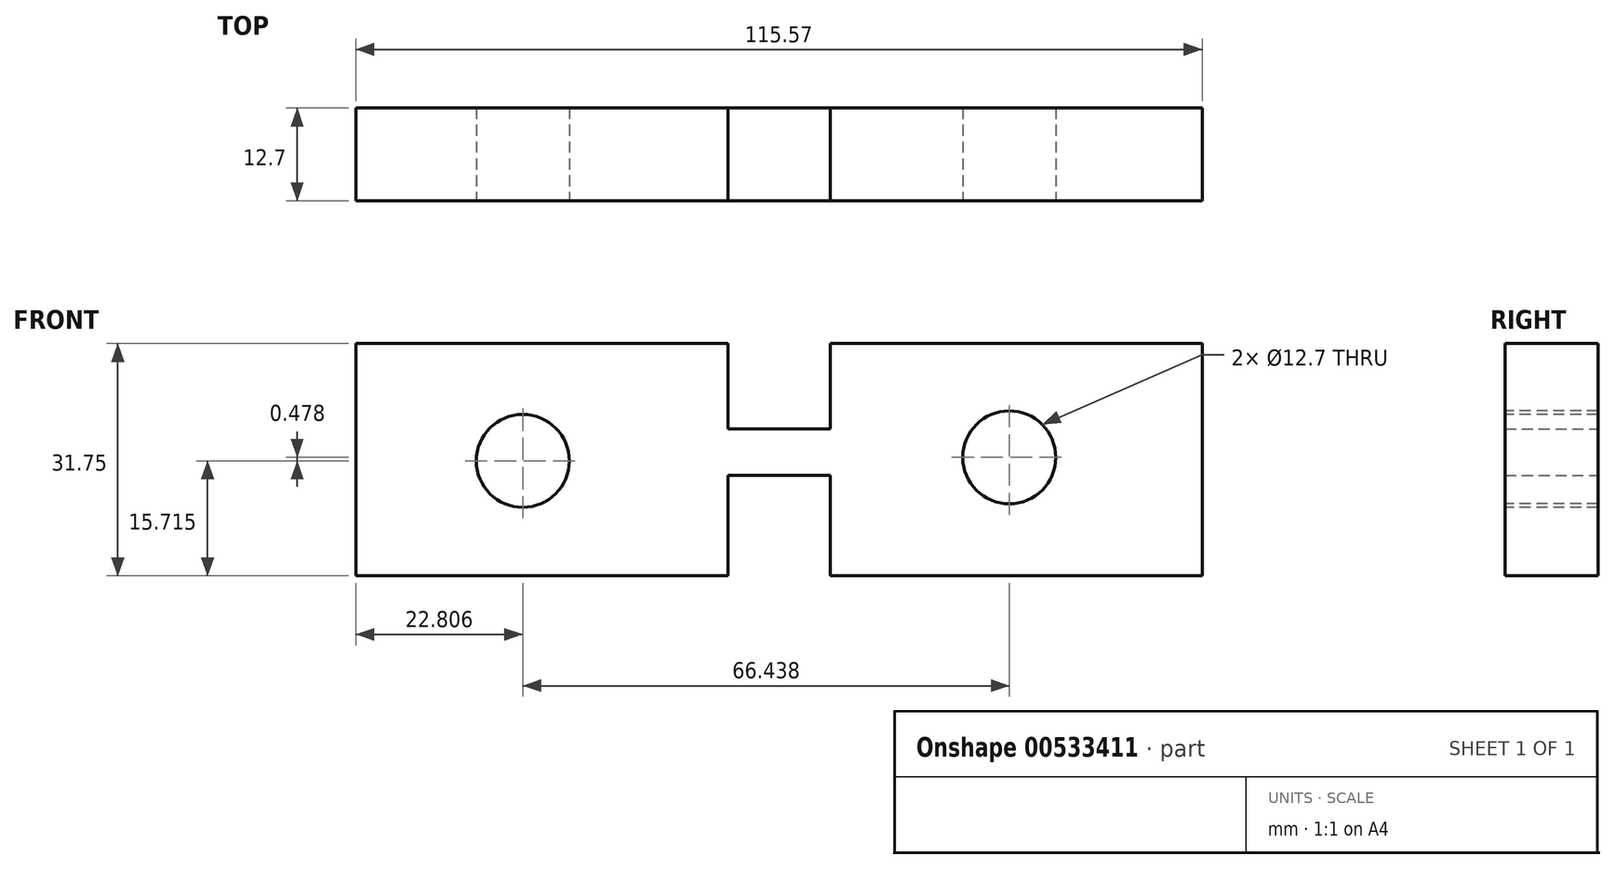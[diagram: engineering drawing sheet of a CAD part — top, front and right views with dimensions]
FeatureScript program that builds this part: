
annotation { "Feature Type Name" : "Feature", "Feature Type Description" : "" }
export const myFeature = defineFeature(function(context is Context, id is Id, definition is map)
    precondition{}
    {
        {
            var Q0;
            Q0=qCreatedBy(makeId("Front.planeOp"),FACE);
            var sketch = newSketch(context, id + "F0", { "sketchPlane" : qUnion([Q0])});
            skLineSegment(sketch, "E0", {"start": v(-13.97, 33.78) * mm, "end": v(0, 33.78) * mm});
            skLineSegment(sketch, "E1", {"start": v(0, 33.78) * mm, "end": v(0, 27.43) * mm});
            skLineSegment(sketch, "E2", {"start": v(0, 27.43) * mm, "end": v(-13.97, 27.43) * mm});
            skLineSegment(sketch, "E3.bottom", {"start": v(0, 45.47) * mm, "end": v(50.8, 45.47) * mm});
            skLineSegment(sketch, "E3.top", {"start": v(0, 13.72) * mm, "end": v(50.8, 13.72) * mm});
            skLineSegment(sketch, "E3.left", {"start": v(0, 45.47) * mm, "end": v(0, 13.72) * mm});
            skLineSegment(sketch, "E3.right", {"start": v(50.8, 45.47) * mm, "end": v(50.8, 13.72) * mm});
            skLineSegment(sketch, "E4", {"start": v(-13.97, 33.78) * mm, "end": v(-13.97, 27.43) * mm});
            skLineSegment(sketch, "E5.bottom", {"start": v(-13.97, 45.47) * mm, "end": v(-64.77, 45.47) * mm});
            skLineSegment(sketch, "E5.top", {"start": v(-13.97, 13.72) * mm, "end": v(-64.77, 13.72) * mm});
            skLineSegment(sketch, "E5.left", {"start": v(-13.97, 45.47) * mm, "end": v(-13.97, 13.72) * mm});
            skLineSegment(sketch, "E5.right", {"start": v(-64.77, 45.47) * mm, "end": v(-64.77, 13.72) * mm});
            skLineSegment(sketch, "E6", {"start": v(50.8, 35.01) * mm, "end": v(72.2, 65.21) * mm});
            skLineSegment(sketch, "E7", {"start": v(72.2, 65.21) * mm, "end": v(83.95, 65.21) * mm});
            skLineSegment(sketch, "E8", {"start": v(83.95, 65.21) * mm, "end": v(80.04, 58.34) * mm});
            skLineSegment(sketch, "E9", {"start": v(80.04, 58.34) * mm, "end": v(72.2, 58.34) * mm});
            skLineSegment(sketch, "E10", {"start": v(72.2, 58.34) * mm, "end": v(50.8, 29.6) * mm});
            skLineSegment(sketch, "E11", {"start": v(-64.77, 34.6) * mm, "end": v(-90.85, 75.15) * mm});
            skLineSegment(sketch, "E12", {"start": v(-90.85, 75.15) * mm, "end": v(-96.78, 71.33) * mm});
            skLineSegment(sketch, "E13", {"start": v(-96.78, 71.33) * mm, "end": v(-90.97, 62.3) * mm});
            skLineSegment(sketch, "E14", {"start": v(-90.97, 62.3) * mm, "end": v(-64.77, 25.7) * mm});
            skLineSegment(sketch, "E15", {"start": v(-90.85, 75.15) * mm, "end": v(-103.8, 66.82) * mm});
            skPoint(sketch, "E15.endSnap0", {"position": v(-93.88, 66.82) * mm});
            skLineSegment(sketch, "E16", {"start": v(-103.8, 66.82) * mm, "end": v(-109.17, 75.15) * mm});
            skLineSegment(sketch, "E17", {"start": v(-109.17, 75.15) * mm, "end": v(-96.78, 83.12) * mm});
            skLineSegment(sketch, "E18", {"start": v(-96.78, 83.12) * mm, "end": v(-90.85, 75.15) * mm});
            skSolve(sketch);
        }
        {
            var Q0;
            {var subQ3=sQuery(id+"F0.wireOp",EDGE,"E5.bottom");Q0=makeQuery(id+"F0.imprint","IMPRINT",FACE,{"disambiguationData":[TD([[makeQuery(id+"F0.imprint","IMPRINT",EDGE,{"derivedFrom":subQ3}),1.0]])]});}
            var Q1;
            {var subQ3=sQuery(id+"F0.wireOp",EDGE,"E3.bottom");Q1=makeQuery(id+"F0.imprint","IMPRINT",FACE,{"disambiguationData":[TD([[makeQuery(id+"F0.imprint","IMPRINT",EDGE,{"derivedFrom":subQ3}),-1.0]])]});}
            var Q2;
            {var subQ0=sQuery(id+"F0.wireOp",EDGE,"E0");Q2=makeQuery(id+"F0.imprint","IMPRINT",FACE,{"disambiguationData":[TD([[makeQuery(id+"F0.imprint","IMPRINT",EDGE,{"derivedFrom":subQ0}),-1.0]])]});}
            extrude(context, id + "F1", {"entities" : qUnion([Q0, Q1, Q2]), "depth" : 12.7 * mm, "offsetDistance" : 25.4 * mm});
        }
        {
            var Q0;
            Q0=makeQuery(id+"F1.opExtrude","CAP_FACE",FACE,{"disambiguationData":[OSD([sQuery(id+"F0.wireOp",EDGE,"E0"),sQuery(id+"F0.wireOp",EDGE,"E2"),sQuery(id+"F0.wireOp",EDGE,"E3.bottom"),sQuery(id+"F0.wireOp",EDGE,"E3.top"),sQuery(id+"F0.wireOp",EDGE,"E3.left"),sQuery(id+"F0.wireOp",EDGE,"E3.right"),sQuery(id+"F0.wireOp",EDGE,"E5.bottom"),sQuery(id+"F0.wireOp",EDGE,"E5.top"),sQuery(id+"F0.wireOp",EDGE,"E5.left"),sQuery(id+"F0.wireOp",EDGE,"E5.right")])],"isStart":false});
            var sketch = newSketch(context, id + "F2", { "sketchPlane" : qUnion([Q0])});
            skCircle(sketch, "E19", {"center": v(-41.96, 29.43) * mm, "radius": 6.35 * mm});
            skCircle(sketch, "E20", {"center": v(24.47, 29.91) * mm, "radius": 6.35 * mm});
            skSolve(sketch);
        }
        {
            var Q0;
            Q0=makeQuery(id+"F2.imprint","IMPRINT",FACE,{"disambiguationData":[TD([[makeQuery(id+"F2.imprint","IMPRINT",EDGE,{"derivedFrom":sQuery(id+"F2.wireOp",EDGE,"E19")}),1.0]])]});
            var Q1;
            Q1=makeQuery(id+"F2.imprint","IMPRINT",FACE,{"disambiguationData":[TD([[makeQuery(id+"F2.imprint","IMPRINT",EDGE,{"derivedFrom":sQuery(id+"F2.wireOp",EDGE,"E20")}),1.0]])]});
            extrude(context, id + "F3", {"entities" : qUnion([Q0, Q1]), "operationType" : NewBodyOperationType.REMOVE, "oppositeDirection" : true, "depth" : 25.4 * mm, "offsetDistance" : 25.4 * mm});
        }
    });
